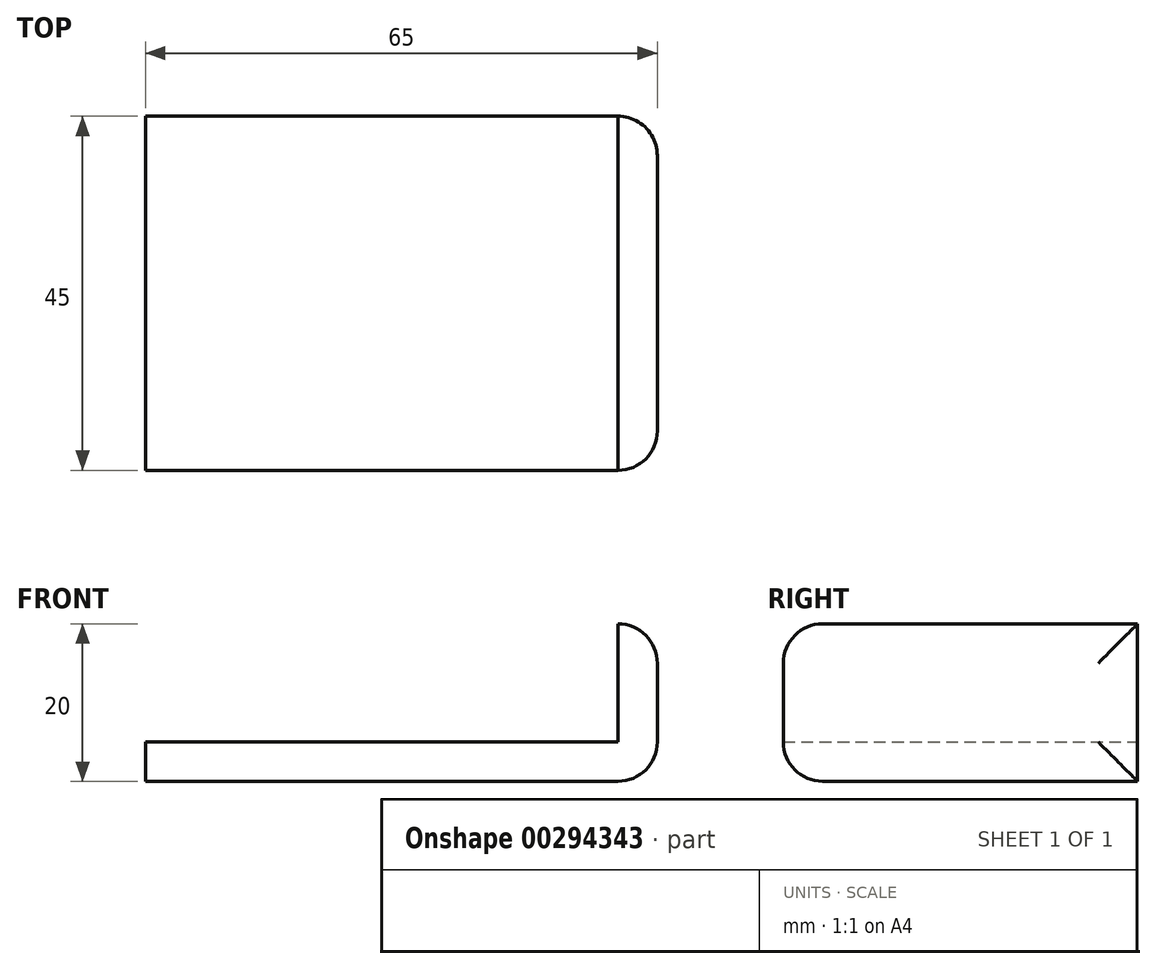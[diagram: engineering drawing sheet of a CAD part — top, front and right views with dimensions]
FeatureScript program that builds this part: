
annotation { "Feature Type Name" : "Feature", "Feature Type Description" : "" }
export const myFeature = defineFeature(function(context is Context, id is Id, definition is map)
    precondition{}
    {
        {
            var Q0;
            Q0=qCreatedBy(makeId("Front.planeOp"),FACE);
            var sketch = newSketch(context, id + "F0", { "sketchPlane" : qUnion([Q0])});
            skLineSegment(sketch, "E0", {"start": v(0, 0) * mm, "end": v(-60, 0) * mm});
            skLineSegment(sketch, "E1", {"start": v(-60, -5) * mm, "end": v(5, -5) * mm});
            skLineSegment(sketch, "E2", {"start": v(5, -5) * mm, "end": v(5, 15) * mm});
            skLineSegment(sketch, "E3", {"start": v(5, 15) * mm, "end": v(0, 15) * mm});
            skLineSegment(sketch, "E4", {"start": v(0, 15) * mm, "end": v(0, 0) * mm});
            skLineSegment(sketch, "E5", {"start": v(-60, 0) * mm, "end": v(-60, -5) * mm});
            skSolve(sketch);
        }
        {
            var Q0;
            Q0=makeQuery(id+"F0.imprint","IMPRINT",FACE,{"disambiguationData":[TD([[makeQuery(id+"F0.imprint","IMPRINT",EDGE,{"derivedFrom":sQuery(id+"F0.wireOp",EDGE,"E0")}),1.0]])]});
            extrude(context, id + "F1", {"entities" : qUnion([Q0]), "depth" : 45 * mm});
        }
        {
            var Q0;
            Q0=makeQuery(id+"F1.opExtrude","SWEPT_EDGE",EDGE,{"disambiguationData":[OSD([sQuery(id+"F0.wireOp",EDGE,"E2"),sQuery(id+"F0.wireOp",EDGE,"E3")])]});
            fillet(context, id + "F2", {"entities" : qUnion([Q0]), "radius" : 5 * mm, "tangentPropagation" : true, "allowEdgeOverflow" : false});
        }
        {
            var Q0;
            Q0=makeQuery(id+"F1.opExtrude","CAP_EDGE",EDGE,{"disambiguationData":[OSD([sQuery(id+"F0.wireOp",EDGE,"E2")])],"isStart":false});
            var Q1;
            Q1=makeQuery(id+"F1.opExtrude","CAP_EDGE",EDGE,{"disambiguationData":[OSD([sQuery(id+"F0.wireOp",EDGE,"E1")])],"isStart":false});
            var Q2;
            {var subQ0=sQuery(id+"F0.wireOp",EDGE,"E3");var subQ1=sQuery(id+"F0.wireOp",EDGE,"E2");Q2=makeQuery(id+"F2.opFillet","BLEND_EDGE",EDGE,{"blendedFrom":[makeQuery(id+"F1.opExtrude","SWEPT_EDGE",EDGE,{"disambiguationData":[OSD([subQ1,subQ0])]}),makeQuery(id+"F1.opExtrude","CAP_FACE",FACE,{"disambiguationData":[OSD([sQuery(id+"F0.wireOp",EDGE,"E0"),sQuery(id+"F0.wireOp",EDGE,"E1"),subQ1,subQ0,sQuery(id+"F0.wireOp",EDGE,"E4"),sQuery(id+"F0.wireOp",EDGE,"E5")])],"isStart":false})],"blendedInto":[makeQuery(id+"F1.opExtrude","CAP_FACE",FACE,{"disambiguationData":[OSD([sQuery(id+"F0.wireOp",EDGE,"E0"),sQuery(id+"F0.wireOp",EDGE,"E1"),subQ1,subQ0,sQuery(id+"F0.wireOp",EDGE,"E4"),sQuery(id+"F0.wireOp",EDGE,"E5")])],"isStart":false})]});}
            var Q3;
            Q3=makeQuery(id+"F1.opExtrude","CAP_EDGE",EDGE,{"disambiguationData":[OSD([sQuery(id+"F0.wireOp",EDGE,"E1")])],"isStart":true});
            var Q4;
            Q4=makeQuery(id+"F1.opExtrude","CAP_EDGE",EDGE,{"disambiguationData":[OSD([sQuery(id+"F0.wireOp",EDGE,"E2")])],"isStart":true});
            var Q5;
            Q5=makeQuery(id+"F1.opExtrude","SWEPT_EDGE",EDGE,{"disambiguationData":[OSD([sQuery(id+"F0.wireOp",EDGE,"E1"),sQuery(id+"F0.wireOp",EDGE,"E2")])]});
            fillet(context, id + "F3", {"entities" : qUnion([Q0, Q1, Q2, Q3, Q4, Q5]), "radius" : 5 * mm, "tangentPropagation" : true, "allowEdgeOverflow" : false});
        }
        {
            var Q0;
            Q0 = qSketchRegion(id + "F0", true);
            extrude(context, id + "F4", {"entities" : qUnion([Q0]), "operationType" : NewBodyOperationType.ADD, "depth" : 25 * mm});
        }
        {
            var Q0;
            Q0=makeQuery(id+"F4.opExtrude","SWEPT_EDGE",EDGE,{"disambiguationData":[OSD([sQuery(id+"F0.wireOp",EDGE,"E2"),sQuery(id+"F0.wireOp",EDGE,"E3")])]});
            var Q1;
            Q1=makeQuery(id+"F4.opExtrude","SWEPT_EDGE",EDGE,{"disambiguationData":[OSD([sQuery(id+"F0.wireOp",EDGE,"E1"),sQuery(id+"F0.wireOp",EDGE,"E2")])]});
            var Q2;
            Q2=makeQuery(id+"F4.opExtrude","CAP_EDGE",EDGE,{"disambiguationData":[OSD([sQuery(id+"F0.wireOp",EDGE,"E2")])],"isStart":true});
            fillet(context, id + "F5", {"entities" : qUnion([Q0, Q1, Q2]), "radius" : 5 * mm, "tangentPropagation" : true, "allowEdgeOverflow" : false});
        }
    });
